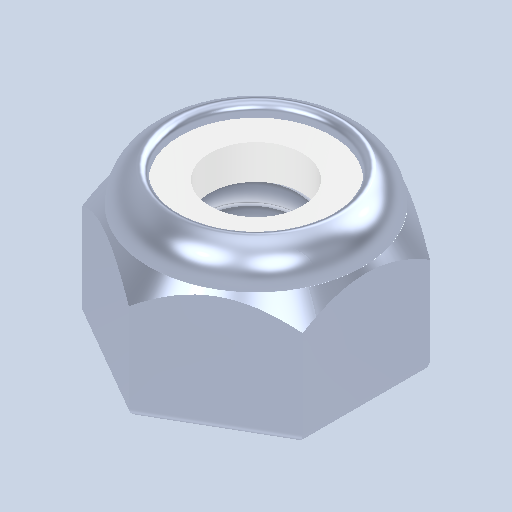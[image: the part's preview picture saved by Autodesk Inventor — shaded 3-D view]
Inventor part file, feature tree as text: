
AUTODESK INVENTOR PART (.ipt)
format: ipt  version: 2023 (Build 270158000, 158)  size: 248,832 bytes
history: native  units: in
note: dims shown in document units (in); Inventor stores cm internally (conversion verified against a paired STEP export)
features: plane x2, other x1, imported_body x1, split x1, thread x1, extrude x1, fillet x1, sketch x1
ambient origin geometry x8: Origin, YZ Plane, XZ Plane, XY Plane, X Axis, Y Axis, Z Axis, Center Point
bodies: Body1 (feature_tree)
feature tree (9):
  parser-record x1  (decoder bookkeeping rows leaked as tree rows — omitted from the tree; the rows remain in map.json)
  imported_body  "Base1"
  plane  "Work Plane1"
  split  "Split1"
  thread  "Thread1"  [1 undecoded]
  plane  "Work Plane2"
  extrude  "Extrusion1"  Depth=0.015in TaperAngle=0.0deg
  fillet  "Fillet1"  Radius=0.015in
  sketch  "Sketch1"  dims[d2=-0.05in d4=0.053in d5=0.0in d6=0.015in]
note: 1 required parameter value undecoded (feature->parameter linkage not recoverable at this tier; creation-order binding heuristic only, values carry confidence <= 0.55)
